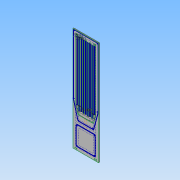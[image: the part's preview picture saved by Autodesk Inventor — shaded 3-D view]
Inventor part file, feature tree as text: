
AUTODESK INVENTOR PART (.ipt)
format: ipt  version: 2013 (Build 170138000, 138)  size: 396,800 bytes
history: native  units: in
note: dims shown in document units (in); Inventor stores cm internally (conversion verified against a paired STEP export)
features: other x14, extrude x3, hole x1, plane x1
ambient origin geometry x8: Origin, YZ Plane, XZ Plane, XY Plane, X Axis, Y Axis, Z Axis, Center Point
bodies: Solid1 (feature_tree)
feature tree (19):
  other  "Blocks"
  extrude  "Stock Extrusion"  Depth=23.8125in
  extrude  "Main rope pocket"  Depth=96.0in
  other  "Side profile reference"
  hole  "Hole1"  [1 undecoded]
  plane  "Work Plane1"
  extrude  "Through Panel Extrusion5"  Depth=58.0in
  other  "Exclaim Point"
  other  "Removal extra wood"
  other  "Stock"
  other  "LEDPocket"
  other  "TwoLineColumn"
  other  "TwoLineColumnEnd"
  other  "15mm Neon profile"
  other  "U Bolt hole and bore"
  other  "U-Bolt holes"
  other  "WeatherProof panel"
  other  "15mm Neon profile:1"
  other  "15mm Neon profile:2"
note: 1 required parameter value undecoded (feature->parameter linkage not recoverable at this tier; creation-order binding heuristic only, values carry confidence <= 0.55)
